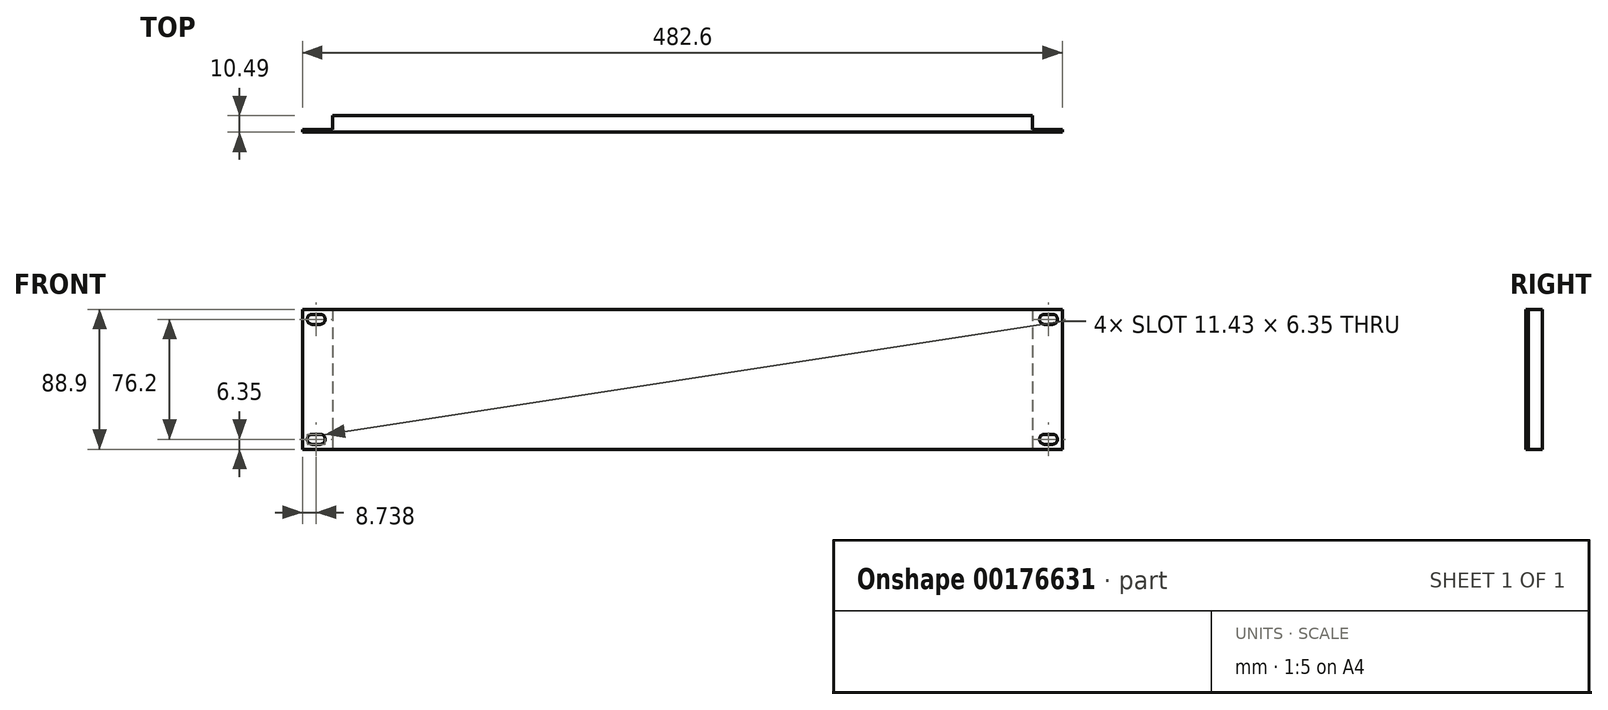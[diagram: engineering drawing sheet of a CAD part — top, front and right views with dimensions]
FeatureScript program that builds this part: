
annotation { "Feature Type Name" : "Feature", "Feature Type Description" : "" }
export const myFeature = defineFeature(function(context is Context, id is Id, definition is map)
    precondition{}
    {
        {
            assignVariable(context, id + "F0", {"name" : "depth", "anyValue" : 8.9});
        }
        {
            var Q0;
            Q0=qCreatedBy(makeId("Front.planeOp"),FACE);
            var sketch = newSketch(context, id + "F1", { "sketchPlane" : qUnion([Q0])});
            skLineSegment(sketch, "E0.bottom", {"start": v(241.3, 44.45) * mm, "end": v(-241.3, 44.45) * mm});
            skLineSegment(sketch, "E0.top", {"start": v(241.3, -44.45) * mm, "end": v(-241.3, -44.45) * mm});
            skLineSegment(sketch, "E0.left", {"start": v(241.3, 44.45) * mm, "end": v(241.3, -44.45) * mm});
            skLineSegment(sketch, "E0.right", {"start": v(-241.3, 44.45) * mm, "end": v(-241.3, -44.45) * mm});
            skPoint(sketch, "E0.middle", {"position": v(0, 0) * mm});
            skLineSegment(sketch, "E1", {"start": v(-232.56, 44.45) * mm, "end": v(-232.56, -44.45) * mm, "construction": true});
            skLineSegment(sketch, "E2", {"start": v(232.56, 44.45) * mm, "end": v(232.56, -44.45) * mm, "construction": true});
            skLineSegment(sketch, "E3", {"start": v(0, 0) * mm, "end": v(-232.56, 0) * mm, "construction": true});
            skLineSegment(sketch, "E4", {"start": v(0, 0) * mm, "end": v(232.56, 0) * mm, "construction": true});
            skLineSegment(sketch, "E5", {"start": v(-235.1, 38.1) * mm, "end": v(-230.02, 38.1) * mm, "construction": true});
            skArc(sketch, "E6", {"start": v(-235.1, 41.28) * mm, "mid": v(-238.28, 38.1) * mm, "end": v(-235.1, 34.93) * mm});
            skArc(sketch, "E7", {"start": v(-230.02, 34.93) * mm, "mid": v(-226.85, 38.1) * mm, "end": v(-230.02, 41.28) * mm});
            skLineSegment(sketch, "E8", {"start": v(-235.1, 41.28) * mm, "end": v(-230.02, 41.28) * mm});
            skLineSegment(sketch, "E9", {"start": v(-235.1, 34.93) * mm, "end": v(-230.02, 34.93) * mm});
            skPoint(sketch, "E10", {"position": v(-232.56, 38.1) * mm});
            skArc(sketch, "E11.MirrorCS", {"start": v(-230.02, -34.93) * mm, "mid": v(-226.85, -38.1) * mm, "end": v(-230.02, -41.28) * mm});
            skLineSegment(sketch, "E12.MirrorCS", {"start": v(-235.1, -41.28) * mm, "end": v(-230.02, -41.28) * mm});
            skArc(sketch, "E13.MirrorCS", {"start": v(-235.1, -41.28) * mm, "mid": v(-238.28, -38.1) * mm, "end": v(-235.1, -34.93) * mm});
            skLineSegment(sketch, "E14.MirrorCS", {"start": v(-235.1, -34.93) * mm, "end": v(-230.02, -34.93) * mm});
            skArc(sketch, "E15.MirrorCS", {"start": v(230.02, 34.93) * mm, "mid": v(226.85, 38.1) * mm, "end": v(230.02, 41.28) * mm});
            skLineSegment(sketch, "E16.MirrorCS", {"start": v(235.1, 41.28) * mm, "end": v(230.02, 41.28) * mm});
            skArc(sketch, "E17.MirrorCS", {"start": v(235.1, 41.28) * mm, "mid": v(238.28, 38.1) * mm, "end": v(235.1, 34.93) * mm});
            skLineSegment(sketch, "E18.MirrorCS", {"start": v(235.1, 34.93) * mm, "end": v(230.02, 34.93) * mm});
            skLineSegment(sketch, "E19.MirrorCS", {"start": v(235.1, -34.93) * mm, "end": v(230.02, -34.93) * mm});
            skArc(sketch, "E20.MirrorCS", {"start": v(235.1, -41.28) * mm, "mid": v(238.28, -38.1) * mm, "end": v(235.1, -34.93) * mm});
            skLineSegment(sketch, "E21.MirrorCS", {"start": v(235.1, -41.28) * mm, "end": v(230.02, -41.28) * mm});
            skArc(sketch, "E22.MirrorCS", {"start": v(230.02, -34.93) * mm, "mid": v(226.85, -38.1) * mm, "end": v(230.02, -41.28) * mm});
            skSolve(sketch);
        }
        {
            var Q0;
            Q0 = qSketchRegion(id + "F1", true);
            extrude(context, id + "F2", {"entities" : qUnion([Q0]), "depth" : 1.59 * mm});
        }
        {
            var Q0;
            Q0=makeQuery(id+"F2.opExtrude","CAP_FACE",FACE,{"disambiguationData":[OSD([sQuery(id+"F1.wireOp",EDGE,"E0.bottom"),sQuery(id+"F1.wireOp",EDGE,"E0.top"),sQuery(id+"F1.wireOp",EDGE,"E0.left"),sQuery(id+"F1.wireOp",EDGE,"E0.right"),sQuery(id+"F1.wireOp",EDGE,"E6"),sQuery(id+"F1.wireOp",EDGE,"E7"),sQuery(id+"F1.wireOp",EDGE,"E8"),sQuery(id+"F1.wireOp",EDGE,"E9"),sQuery(id+"F1.wireOp",EDGE,"E11.MirrorCS"),sQuery(id+"F1.wireOp",EDGE,"E12.MirrorCS"),sQuery(id+"F1.wireOp",EDGE,"E13.MirrorCS"),sQuery(id+"F1.wireOp",EDGE,"E14.MirrorCS"),sQuery(id+"F1.wireOp",EDGE,"E15.MirrorCS"),sQuery(id+"F1.wireOp",EDGE,"E16.MirrorCS"),sQuery(id+"F1.wireOp",EDGE,"E17.MirrorCS"),sQuery(id+"F1.wireOp",EDGE,"E18.MirrorCS"),sQuery(id+"F1.wireOp",EDGE,"E19.MirrorCS"),sQuery(id+"F1.wireOp",EDGE,"E20.MirrorCS"),sQuery(id+"F1.wireOp",EDGE,"E21.MirrorCS"),sQuery(id+"F1.wireOp",EDGE,"E22.MirrorCS")])],"isStart":true});
            var sketch = newSketch(context, id + "F3", { "sketchPlane" : qUnion([Q0])});
            skLineSegment(sketch, "E23.bottom", {"start": v(-222.25, 44.45) * mm, "end": v(222.25, 44.45) * mm});
            skLineSegment(sketch, "E23.top", {"start": v(-222.25, -44.45) * mm, "end": v(222.25, -44.45) * mm});
            skLineSegment(sketch, "E23.left", {"start": v(-222.25, 44.45) * mm, "end": v(-222.25, -44.45) * mm});
            skLineSegment(sketch, "E23.right", {"start": v(222.25, 44.45) * mm, "end": v(222.25, -44.45) * mm});
            skPoint(sketch, "E23.middle", {"position": v(0, 0) * mm});
            skSolve(sketch);
        }
        {
            var Q0;
            Q0 = qSketchRegion(id + "F3", true);
            extrude(context, id + "F4", {"entities" : qUnion([Q0]), "operationType" : NewBodyOperationType.ADD, "depth" : (getVariable(context, 'depth')) * mm});
        }
        {
            var Q0;
            {var subQ0=sQuery(id+"F1.wireOp",EDGE,"E21.MirrorCS");var subQ1=sQuery(id+"F1.wireOp",EDGE,"E20.MirrorCS");var subQ2=sQuery(id+"F1.wireOp",EDGE,"E19.MirrorCS");var subQ3=sQuery(id+"F1.wireOp",EDGE,"E18.MirrorCS");var subQ4=sQuery(id+"F1.wireOp",EDGE,"E16.MirrorCS");var subQ5=sQuery(id+"F1.wireOp",EDGE,"E0.bottom");var subQ6=sQuery(id+"F1.wireOp",EDGE,"E15.MirrorCS");var subQ7=sQuery(id+"F1.wireOp",EDGE,"E22.MirrorCS");var subQ8=sQuery(id+"F1.wireOp",EDGE,"E0.top");var subQ9=sQuery(id+"F1.wireOp",EDGE,"E17.MirrorCS");var subQ10=sQuery(id+"F1.wireOp",EDGE,"E0.left");Q0=makeQuery(id+"F4.boolean.opBoolean","SPLIT",FACE,{"disambiguationData":[TD([makeQuery(id+"F2.opExtrude","SWEPT_FACE",FACE,{"disambiguationData":[OSD([subQ10])]})])],"derivedFrom":makeQuery(id+"F2.opExtrude","CAP_FACE",FACE,{"disambiguationData":[OSD([subQ5,subQ8,subQ10,sQuery(id+"F1.wireOp",EDGE,"E0.right"),sQuery(id+"F1.wireOp",EDGE,"E6"),sQuery(id+"F1.wireOp",EDGE,"E7"),sQuery(id+"F1.wireOp",EDGE,"E8"),sQuery(id+"F1.wireOp",EDGE,"E9"),sQuery(id+"F1.wireOp",EDGE,"E11.MirrorCS"),sQuery(id+"F1.wireOp",EDGE,"E12.MirrorCS"),sQuery(id+"F1.wireOp",EDGE,"E13.MirrorCS"),sQuery(id+"F1.wireOp",EDGE,"E14.MirrorCS"),subQ6,subQ4,subQ9,subQ3,subQ2,subQ1,subQ0,subQ7])],"isStart":true})});}
            var sketch = newSketch(context, id + "F5", { "sketchPlane" : qUnion([Q0])});
            skLineSegment(sketch, "E24", {"start": v(-232.56, -34.93) * mm, "end": v(-232.56, -41.28) * mm, "construction": true});
            skSolve(sketch);
        }
    });
